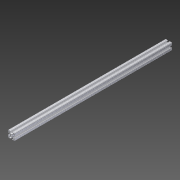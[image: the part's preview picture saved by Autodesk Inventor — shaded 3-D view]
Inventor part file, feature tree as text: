
AUTODESK INVENTOR PART (.ipt)
format: ipt  version: 2013 (Build 170138000, 138)  size: 293,376 bytes
history: native  units: in
note: dims shown in document units (in); Inventor stores cm internally (conversion verified against a paired STEP export)
features: extrude x2, imported_body x1, sketch x1
ambient origin geometry x8: Origin, YZ Plane, XZ Plane, XY Plane, X Axis, Y Axis, Z Axis, Center Point
feature tree (4):
  extrude  "Extrude1"  [1 undecoded]
  extrude  "Extrusion1"  [1 undecoded]
  imported_body  "Base1"
  sketch  "Sketch1"  dims[d0=11.5in d1=0.0in]
note: 2 required parameter values undecoded (feature->parameter linkage not recoverable at this tier; creation-order binding heuristic only, values carry confidence <= 0.55)
